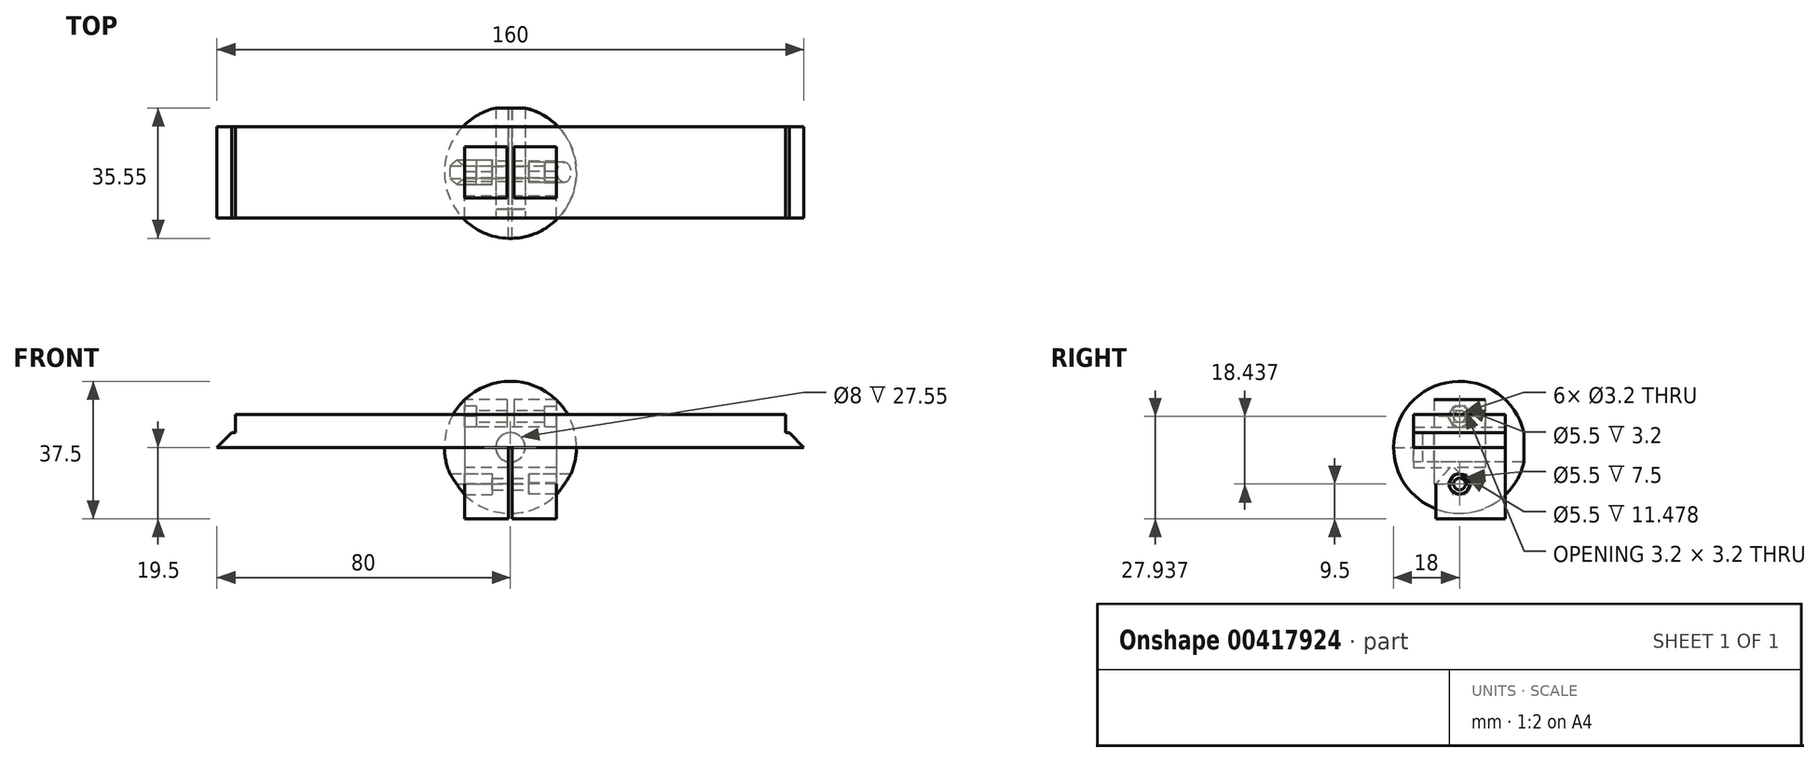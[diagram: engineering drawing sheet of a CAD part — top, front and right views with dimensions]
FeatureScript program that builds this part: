
annotation { "Feature Type Name" : "Feature", "Feature Type Description" : "" }
export const myFeature = defineFeature(function(context is Context, id is Id, definition is map)
    precondition{}
    {
        {
            var Q0;
            Q0=qCreatedBy(makeId("Right.planeOp"),FACE);
            var sketch = newSketch(context, id + "F0", { "sketchPlane" : qUnion([Q0])});
            skLineSegment(sketch, "E0.bottom", {"start": v(-7, 13) * mm, "end": v(7, 13) * mm});
            skLineSegment(sketch, "E0.top", {"start": v(-7, -10) * mm, "end": v(3, -10) * mm});
            skLineSegment(sketch, "E0.left", {"start": v(-7, 13) * mm, "end": v(-7, -10) * mm});
            skLineSegment(sketch, "E0.right", {"start": v(7, 13) * mm, "end": v(7, -5.5) * mm});
            skPoint(sketch, "E1", {"position": v(0, 13) * mm});
            skLineSegment(sketch, "E2.bottom", {"start": v(-23.43, 4) * mm, "end": v(36.95, 4) * mm, "construction": true});
            skLineSegment(sketch, "E2.top", {"start": v(-23.43, -4) * mm, "end": v(36.95, -4) * mm, "construction": true});
            skLineSegment(sketch, "E2.left", {"start": v(-23.43, 4) * mm, "end": v(-23.43, -4) * mm, "construction": true});
            skLineSegment(sketch, "E2.right", {"start": v(36.95, 4) * mm, "end": v(36.95, -4) * mm, "construction": true});
            skPoint(sketch, "E3", {"position": v(-23.43, 0) * mm});
            skLineSegment(sketch, "E4", {"start": v(7, -5.5) * mm, "end": v(-1.5, -5.5) * mm});
            skLineSegment(sketch, "E5", {"start": v(-1.5, -5.5) * mm, "end": v(3, -10) * mm});
            skSolve(sketch);
        }
        {
            var Q0;
            Q0=makeQuery(id+"F0.imprint","IMPRINT",FACE,{"disambiguationData":[TD([[makeQuery(id+"F0.imprint","IMPRINT",EDGE,{"derivedFrom":sQuery(id+"F0.wireOp",EDGE,"E0.bottom")}),-1.0]])]});
            extrude(context, id + "F1", {"entities" : qUnion([Q0]), "endBound" : BoundingType.SYMMETRIC, "depth" : 25 * mm});
        }
        {
            var Q0;
            Q0=makeQuery(id+"F1.opExtrude","SWEPT_FACE",FACE,{"disambiguationData":[OSD([sQuery(id+"F0.wireOp",EDGE,"E0.left")])]});
            var sketch = newSketch(context, id + "F2", { "sketchPlane" : qUnion([Q0])});
            skCircle(sketch, "E6", {"center": v(0, 0) * mm, "radius": 4 * mm});
            skLineSegment(sketch, "E7", {"start": v(-1, 3.87) * mm, "end": v(-1, 13) * mm});
            skLineSegment(sketch, "E8", {"start": v(-1, 13) * mm, "end": v(1, 13) * mm});
            skLineSegment(sketch, "E9", {"start": v(1, 13) * mm, "end": v(1, 3.87) * mm});
            skSolve(sketch);
        }
        {
            var Q0;
            {var subQ0=sQuery(id+"F2.wireOp",EDGE,"E7");Q0=makeQuery(id+"F2.imprint","IMPRINT",FACE,{"disambiguationData":[TD([[makeQuery(id+"F2.imprint","IMPRINT",EDGE,{"derivedFrom":subQ0}),-1.0]])]});}
            var Q1;
            {var subQ0=sQuery(id+"F2.wireOp",EDGE,"E6");var subQ1=makeQuery(id+"F2.imprint","INTERSECT",VERTEX,{"derivedFrom":[subQ0,sQuery(id+"F2.wireOp",EDGE,"E7")]});Q1=makeQuery(id+"F2.imprint","IMPRINT",FACE,{"disambiguationData":[TD([[makeQuery(id+"F2.imprint","IMPRINT",EDGE,{"disambiguationData":[TD([[subQ1,1.0]])],"derivedFrom":subQ0}),1.0]])]});}
            extrude(context, id + "F3", {"entities" : qUnion([Q0, Q1]), "operationType" : NewBodyOperationType.REMOVE, "endBound" : BoundingType.THROUGH_ALL, "oppositeDirection" : true, "depth" : 25 * mm});
        }
        {
            var Q0;
            Q0=makeQuery(id+"F1.opExtrude","CAP_FACE",FACE,{"disambiguationData":[OSD([sQuery(id+"F0.wireOp",EDGE,"E0.bottom"),sQuery(id+"F0.wireOp",EDGE,"E0.top"),sQuery(id+"F0.wireOp",EDGE,"E0.left"),sQuery(id+"F0.wireOp",EDGE,"E0.right"),sQuery(id+"F0.wireOp",EDGE,"E4"),sQuery(id+"F0.wireOp",EDGE,"E5")])],"isStart":true});
            var sketch = newSketch(context, id + "F4", { "sketchPlane" : qUnion([Q0])});
            skCircle(sketch, "E10", {"center": v(0, 8.44) * mm, "radius": 1.6 * mm});
            skPoint(sketch, "E10.centerSnap0", {"position": v(0, 13) * mm});
            skLineSegment(sketch, "E11.0", {"start": v(-7, 13) * mm, "end": v(-7, 3.87) * mm, "construction": true});
            skPoint(sketch, "E12", {"position": v(-7, 8.44) * mm});
            skSolve(sketch);
        }
        {
            var Q0;
            Q0=makeQuery(id+"F4.imprint","IMPRINT",FACE,{"disambiguationData":[TD([[makeQuery(id+"F4.imprint","IMPRINT",EDGE,{"derivedFrom":sQuery(id+"F4.wireOp",EDGE,"E10")}),1.0]])]});
            extrude(context, id + "F5", {"entities" : qUnion([Q0]), "operationType" : NewBodyOperationType.REMOVE, "endBound" : BoundingType.THROUGH_ALL, "oppositeDirection" : true, "depth" : 25 * mm});
        }
        {
            var Q0;
            Q0=makeQuery(id+"F1.opExtrude","CAP_FACE",FACE,{"disambiguationData":[OSD([sQuery(id+"F0.wireOp",EDGE,"E0.bottom"),sQuery(id+"F0.wireOp",EDGE,"E0.top"),sQuery(id+"F0.wireOp",EDGE,"E0.left"),sQuery(id+"F0.wireOp",EDGE,"E0.right"),sQuery(id+"F0.wireOp",EDGE,"E4"),sQuery(id+"F0.wireOp",EDGE,"E5")])],"isStart":true});
            var sketch = newSketch(context, id + "F6", { "sketchPlane" : qUnion([Q0])});
            skCircle(sketch, "E13.0", {"center": v(0, 8.44) * mm, "radius": 1.6 * mm, "construction": true});
            skCircle(sketch, "E14.cCircle", {"center": v(0, 8.44) * mm, "radius": 2.85 * mm, "construction": true});
            skLineSegment(sketch, "E14.0", {"start": v(1.65, 5.59) * mm, "end": v(-1.65, 5.59) * mm});
            skLineSegment(sketch, "E14.1", {"start": v(-1.65, 5.59) * mm, "end": v(-3.3, 8.44) * mm});
            skLineSegment(sketch, "E14.2", {"start": v(-3.3, 8.44) * mm, "end": v(-1.65, 11.29) * mm});
            skLineSegment(sketch, "E14.3", {"start": v(-1.65, 11.29) * mm, "end": v(1.65, 11.29) * mm});
            skLineSegment(sketch, "E14.4", {"start": v(1.65, 11.29) * mm, "end": v(3.3, 8.44) * mm});
            skLineSegment(sketch, "E14.5", {"start": v(3.3, 8.44) * mm, "end": v(1.65, 5.59) * mm});
            skPoint(sketch, "E14.0.midPoint", {"position": v(0, 5.59) * mm});
            skSolve(sketch);
        }
        {
            var Q0;
            Q0=makeQuery(id+"F6.imprint","IMPRINT",FACE,{"disambiguationData":[TD([[makeQuery(id+"F6.imprint","IMPRINT",EDGE,{"derivedFrom":sQuery(id+"F6.wireOp",EDGE,"E14.0")}),-1.0]])]});
            extrude(context, id + "F7", {"entities" : qUnion([Q0]), "operationType" : NewBodyOperationType.REMOVE, "oppositeDirection" : true, "depth" : 3.2 * mm});
        }
        {
            var Q0;
            Q0=makeQuery(id+"F1.opExtrude","CAP_FACE",FACE,{"disambiguationData":[OSD([sQuery(id+"F0.wireOp",EDGE,"E0.bottom"),sQuery(id+"F0.wireOp",EDGE,"E0.top"),sQuery(id+"F0.wireOp",EDGE,"E0.left"),sQuery(id+"F0.wireOp",EDGE,"E0.right"),sQuery(id+"F0.wireOp",EDGE,"E4"),sQuery(id+"F0.wireOp",EDGE,"E5")])],"isStart":false});
            var sketch = newSketch(context, id + "F8", { "sketchPlane" : qUnion([Q0])});
            skCircle(sketch, "E15", {"center": v(0, 8.44) * mm, "radius": 2.75 * mm});
            skSolve(sketch);
        }
        {
            var Q0;
            Q0=qSketchRegion(id+"F8",true);
            extrude(context, id + "F9", {"entities" : qUnion([Q0]), "operationType" : NewBodyOperationType.REMOVE, "oppositeDirection" : true, "depth" : 3.2 * mm});
        }
        {
            var Q0;
            Q0=qCreatedBy(makeId("Right.planeOp"),FACE);
            var sketch = newSketch(context, id + "F10", { "sketchPlane" : qUnion([Q0])});
            skLineSegment(sketch, "E16.bottom", {"start": v(-31.87, 4) * mm, "end": v(35.54, 4) * mm, "construction": true});
            skLineSegment(sketch, "E16.top", {"start": v(-31.87, -4) * mm, "end": v(35.54, -4) * mm, "construction": true});
            skLineSegment(sketch, "E16.left", {"start": v(-31.87, 4) * mm, "end": v(-31.87, -4) * mm, "construction": true});
            skLineSegment(sketch, "E16.right", {"start": v(35.54, 4) * mm, "end": v(35.54, -4) * mm, "construction": true});
            skPoint(sketch, "E17", {"position": v(-31.87, 0) * mm});
            skLineSegment(sketch, "E18.bottom", {"start": v(-12.5, 5.5) * mm, "end": v(12.5, 5.5) * mm});
            skLineSegment(sketch, "E18.top", {"start": v(-6.5, -19.5) * mm, "end": v(12.5, -19.5) * mm});
            skLineSegment(sketch, "E18.left", {"start": v(-12.5, 5.5) * mm, "end": v(-12.5, -5.5) * mm});
            skLineSegment(sketch, "E18.right", {"start": v(12.5, 5.5) * mm, "end": v(12.5, -19.5) * mm});
            skLineSegment(sketch, "E19", {"start": v(-12.5, -5.5) * mm, "end": v(-2.5, -5.5) * mm});
            skLineSegment(sketch, "E20", {"start": v(-2.5, -5.5) * mm, "end": v(-6.5, -10) * mm});
            skLineSegment(sketch, "E21", {"start": v(-6.5, -10) * mm, "end": v(-6.5, -19.5) * mm});
            skPoint(sketch, "E22", {"position": v(0, 5.5) * mm});
            skPoint(sketch, "E23", {"position": v(-12.5, 0) * mm});
            skSolve(sketch);
        }
        {
            var Q0;
            Q0=makeQuery(id+"F10.imprint","IMPRINT",FACE,{"disambiguationData":[TD([[makeQuery(id+"F10.imprint","IMPRINT",EDGE,{"derivedFrom":sQuery(id+"F10.wireOp",EDGE,"E18.bottom")}),-1.0]])]});
            extrude(context, id + "F11", {"entities" : qUnion([Q0]), "endBound" : BoundingType.SYMMETRIC, "depth" : 25 * mm});
        }
        {
            var Q0;
            Q0=makeQuery(id+"F11.opExtrude","SWEPT_FACE",FACE,{"disambiguationData":[OSD([sQuery(id+"F10.wireOp",EDGE,"E18.left")])]});
            var sketch = newSketch(context, id + "F12", { "sketchPlane" : qUnion([Q0])});
            skCircle(sketch, "E24", {"center": v(0, 0) * mm, "radius": 4 * mm});
            skSolve(sketch);
        }
        {
            var Q0;
            Q0=makeQuery(id+"F12.imprint","IMPRINT",FACE,{"disambiguationData":[TD([[makeQuery(id+"F12.imprint","IMPRINT",EDGE,{"derivedFrom":sQuery(id+"F12.wireOp",EDGE,"E24")}),1.0]])]});
            extrude(context, id + "F13", {"entities" : qUnion([Q0]), "operationType" : NewBodyOperationType.REMOVE, "endBound" : BoundingType.THROUGH_ALL, "oppositeDirection" : true, "depth" : 25 * mm});
        }
        {
            var Q0;
            Q0=qCreatedBy(makeId("Top.planeOp"),FACE);
            var sketch = newSketch(context, id + "F14", { "sketchPlane" : qUnion([Q0])});
            skArc(sketch, "E25", {"start": v(0, 18) * mm, "mid": v(-18, 0) * mm, "end": v(0, -18) * mm});
            skLineSegment(sketch, "E26", {"start": v(0, -18) * mm, "end": v(0, 18) * mm});
            skSolve(sketch);
        }
        {
            var Q0;
            Q0=makeQuery(id+"F14.imprint","IMPRINT",FACE,{"disambiguationData":[TD([[makeQuery(id+"F14.imprint","IMPRINT",EDGE,{"derivedFrom":sQuery(id+"F14.wireOp",EDGE,"E25")}),1.0]])]});
            var Q1;
            Q1=sQuery(id+"F14.wireOp",EDGE,"E26");
            revolve(context, id + "F15", {"entities" : qUnion([Q0]), "axis" : qUnion([Q1]), "revolveType" : RevolveType.FULL});
        }
        {
            var Q0;
            Q0=qCreatedBy(makeId("Front.planeOp"),FACE);
            var sketch = newSketch(context, id + "F16", { "sketchPlane" : qUnion([Q0])});
            skCircle(sketch, "E27", {"center": v(0, 0) * mm, "radius": 4 * mm});
            skSolve(sketch);
        }
        {
            var Q0;
            Q0=qSketchRegion(id+"F16",true);
            extrude(context, id + "F17", {"entities" : qUnion([Q0]), "operationType" : NewBodyOperationType.REMOVE, "oppositeDirection" : true, "depth" : 30 * mm, "hasSecondDirection" : true, "secondDirectionOppositeDirection" : false, "secondDirectionDepth" : 10 * mm});
        }
        {
            var Q0;
            Q0=qCreatedBy(makeId("Top.planeOp"),FACE);
            var sketch = newSketch(context, id + "F18", { "sketchPlane" : qUnion([Q0])});
            skLineSegment(sketch, "E28.bottom", {"start": v(-0.5, -18) * mm, "end": v(0.5, -18) * mm});
            skLineSegment(sketch, "E28.top", {"start": v(-0.5, 17.43) * mm, "end": v(0.5, 17.43) * mm});
            skLineSegment(sketch, "E28.left", {"start": v(-0.5, -18) * mm, "end": v(-0.5, 17.43) * mm});
            skLineSegment(sketch, "E28.right", {"start": v(0.5, -18) * mm, "end": v(0.5, 17.43) * mm});
            skPoint(sketch, "E29", {"position": v(0, 17.43) * mm});
            skPoint(sketch, "E30", {"position": v(0, -18) * mm});
            skArc(sketch, "E31", {"start": v(-4.5, 17.43) * mm, "mid": v(0, -18) * mm, "end": v(4.5, 17.43) * mm, "construction": true});
            skSolve(sketch);
        }
        {
            var Q0;
            Q0=makeQuery(id+"F18.imprint","IMPRINT",FACE,{"disambiguationData":[TD([[makeQuery(id+"F18.imprint","IMPRINT",EDGE,{"derivedFrom":sQuery(id+"F18.wireOp",EDGE,"E28.bottom")}),1.0]])]});
            extrude(context, id + "F19", {"entities" : qUnion([Q0]), "operationType" : NewBodyOperationType.REMOVE, "endBound" : BoundingType.THROUGH_ALL, "oppositeDirection" : true, "depth" : 25 * mm});
        }
        {
            var Q0;
            Q0=qCreatedBy(makeId("Right.planeOp"),FACE);
            var sketch = newSketch(context, id + "F20", { "sketchPlane" : qUnion([Q0])});
            skCircle(sketch, "E32", {"center": v(0, -10) * mm, "radius": 1.6 * mm});
            skSolve(sketch);
        }
        {
            var Q0;
            Q0=qSketchRegion(id+"F20",true);
            extrude(context, id + "F21", {"entities" : qUnion([Q0]), "operationType" : NewBodyOperationType.REMOVE, "endBound" : BoundingType.SYMMETRIC, "oppositeDirection" : true, "depth" : 29 * mm});
        }
        {
            var Q0;
            Q0=qCreatedBy(makeId("Right.planeOp"),FACE);
            cPlane(context, id + "F22", {"entities" : qUnion([Q0]), "cplaneType" : CPlaneType.OFFSET, "offset" : 5 * mm, "width" : 150 * mm, "height" : 150 * mm});
        }
        {
            var Q0;
            Q0=qCreatedBy(id+"F22.planeOp",FACE);
            var sketch = newSketch(context, id + "F23", { "sketchPlane" : qUnion([Q0])});
            skCircle(sketch, "E33.0", {"center": v(0, -10) * mm, "radius": 1.6 * mm, "construction": true});
            skCircle(sketch, "E34", {"center": v(0, -10) * mm, "radius": 2.75 * mm});
            skSolve(sketch);
        }
        {
            var Q0;
            Q0=qSketchRegion(id+"F23",true);
            extrude(context, id + "F24", {"entities" : qUnion([Q0]), "operationType" : NewBodyOperationType.REMOVE, "endBound" : BoundingType.THROUGH_ALL, "depth" : 25 * mm});
        }
        {
            var Q0;
            Q0=qCreatedBy(makeId("Right.planeOp"),FACE);
            cPlane(context, id + "F25", {"entities" : qUnion([Q0]), "cplaneType" : CPlaneType.OFFSET, "offset" : 5 * mm, "oppositeDirection" : true, "width" : 150 * mm, "height" : 150 * mm});
        }
        {
            var Q0;
            Q0=qCreatedBy(id+"F25.planeOp",FACE);
            var sketch = newSketch(context, id + "F26", { "sketchPlane" : qUnion([Q0])});
            skCircle(sketch, "E35.0", {"center": v(0.04, -10.02) * mm, "radius": 1.6 * mm, "construction": true});
            skCircle(sketch, "E36.cCircle", {"center": v(0.04, -10.02) * mm, "radius": 2.9 * mm, "construction": true});
            skLineSegment(sketch, "E36.0", {"start": v(1.72, -12.93) * mm, "end": v(-1.63, -12.93) * mm});
            skLineSegment(sketch, "E36.1", {"start": v(-1.63, -12.92) * mm, "end": v(-3.3, -10.02) * mm});
            skLineSegment(sketch, "E36.2", {"start": v(-3.3, -10.02) * mm, "end": v(-1.63, -7.12) * mm});
            skLineSegment(sketch, "E36.3", {"start": v(-1.63, -7.12) * mm, "end": v(1.72, -7.12) * mm});
            skLineSegment(sketch, "E36.4", {"start": v(1.72, -7.13) * mm, "end": v(3.4, -10.02) * mm});
            skLineSegment(sketch, "E36.5", {"start": v(3.4, -10.03) * mm, "end": v(1.72, -12.93) * mm});
            skPoint(sketch, "E36.0.midPoint", {"position": v(0.04, -12.93) * mm});
            skSolve(sketch);
        }
        {
            var Q0;
            Q0=qSketchRegion(id+"F26",true);
            extrude(context, id + "F27", {"entities" : qUnion([Q0]), "operationType" : NewBodyOperationType.REMOVE, "endBound" : BoundingType.THROUGH_ALL, "oppositeDirection" : true, "depth" : 25 * mm});
        }
        {
            var Q0;
            Q0=qCreatedBy(makeId("Front.planeOp"),FACE);
            var sketch = newSketch(context, id + "F28", { "sketchPlane" : qUnion([Q0])});
            skLineSegment(sketch, "E37.bottom", {"start": v(-80, 0) * mm, "end": v(80, 0) * mm});
            skLineSegment(sketch, "E37.top", {"start": v(-76, 4) * mm, "end": v(76, 4) * mm});
            skLineSegment(sketch, "E38", {"start": v(-80, 0) * mm, "end": v(-76, 4) * mm});
            skLineSegment(sketch, "E39", {"start": v(-75, 4) * mm, "end": v(-75, 9) * mm});
            skLineSegment(sketch, "E40", {"start": v(-75, 9) * mm, "end": v(75, 9) * mm});
            skLineSegment(sketch, "E41", {"start": v(75, 9) * mm, "end": v(75, 4) * mm});
            skLineSegment(sketch, "E42", {"start": v(80, 0) * mm, "end": v(76, 4) * mm});
            skPoint(sketch, "E43", {"position": v(0, 9) * mm});
            skPoint(sketch, "E44", {"position": v(0, 0) * mm});
            skSolve(sketch);
        }
        {
            var Q0;
            {var subQ0=sQuery(id+"F28.wireOp",EDGE,"E39");Q0=makeQuery(id+"F28.imprint","IMPRINT",FACE,{"disambiguationData":[TD([[makeQuery(id+"F28.imprint","IMPRINT",EDGE,{"derivedFrom":subQ0}),-1.0]])]});}
            var Q1;
            Q1=makeQuery(id+"F28.imprint","IMPRINT",FACE,{"disambiguationData":[TD([[makeQuery(id+"F28.imprint","IMPRINT",EDGE,{"derivedFrom":sQuery(id+"F28.wireOp",EDGE,"E37.bottom")}),1.0]])]});
            extrude(context, id + "F29", {"entities" : qUnion([Q0, Q1]), "endBound" : BoundingType.SYMMETRIC, "depth" : 25 * mm});
        }
    });
